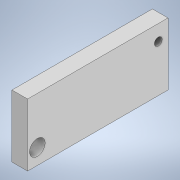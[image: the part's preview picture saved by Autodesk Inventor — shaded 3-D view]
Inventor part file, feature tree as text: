
AUTODESK INVENTOR PART (.ipt)
format: ipt  version: 2021 (Build 250183000, 183)  size: 124,928 bytes
history: native  units: in
note: dims shown in document units (in); Inventor stores cm internally (conversion verified against a paired STEP export)
features: hole x3, sketch x2, projected_geometry x2, extrude x1
ambient origin geometry x8: Origin, YZ Plane, XZ Plane, XY Plane, X Axis, Y Axis, Z Axis, Center Point
bodies: Solid1 (feature_tree)
feature tree (8):
  sketch  "Sketch2"  dims[d0=2.0in d1=4.5in]
  extrude  "Extrusion1"  Depth=4.5in
  hole  "Hole1"  [1 undecoded]
  hole  "Hole2"  [1 undecoded]
  hole  "Hole3"  [1 undecoded]
  sketch  "Sketch3"  dims[d2=3.875in d3=1.0in d4=0.5in d5=0.3125in d6=0.5in d7=0.0in d8=0.25in d9=0.75in d10=0.375in d11=0.25in d12=0.5635in d13=0.75in d14=0.8108in d15=0.5in d16=0.5in d17=0.75in d18=0.375in d19=0.25in d20=0.5635in d21=0.75in d22=0.8108in d23=2.5in d24=0.75in d25=0.196in d26=0.5in d27=0.375in d28=0.25in d29=0.5635in d30=0.75in d31=0.8108in]
  projected_geometry  "Projected Loop1"
  projected_geometry  "Projected Loop2"
note: 3 required parameter values undecoded (feature->parameter linkage not recoverable at this tier; creation-order binding heuristic only, values carry confidence <= 0.55)
